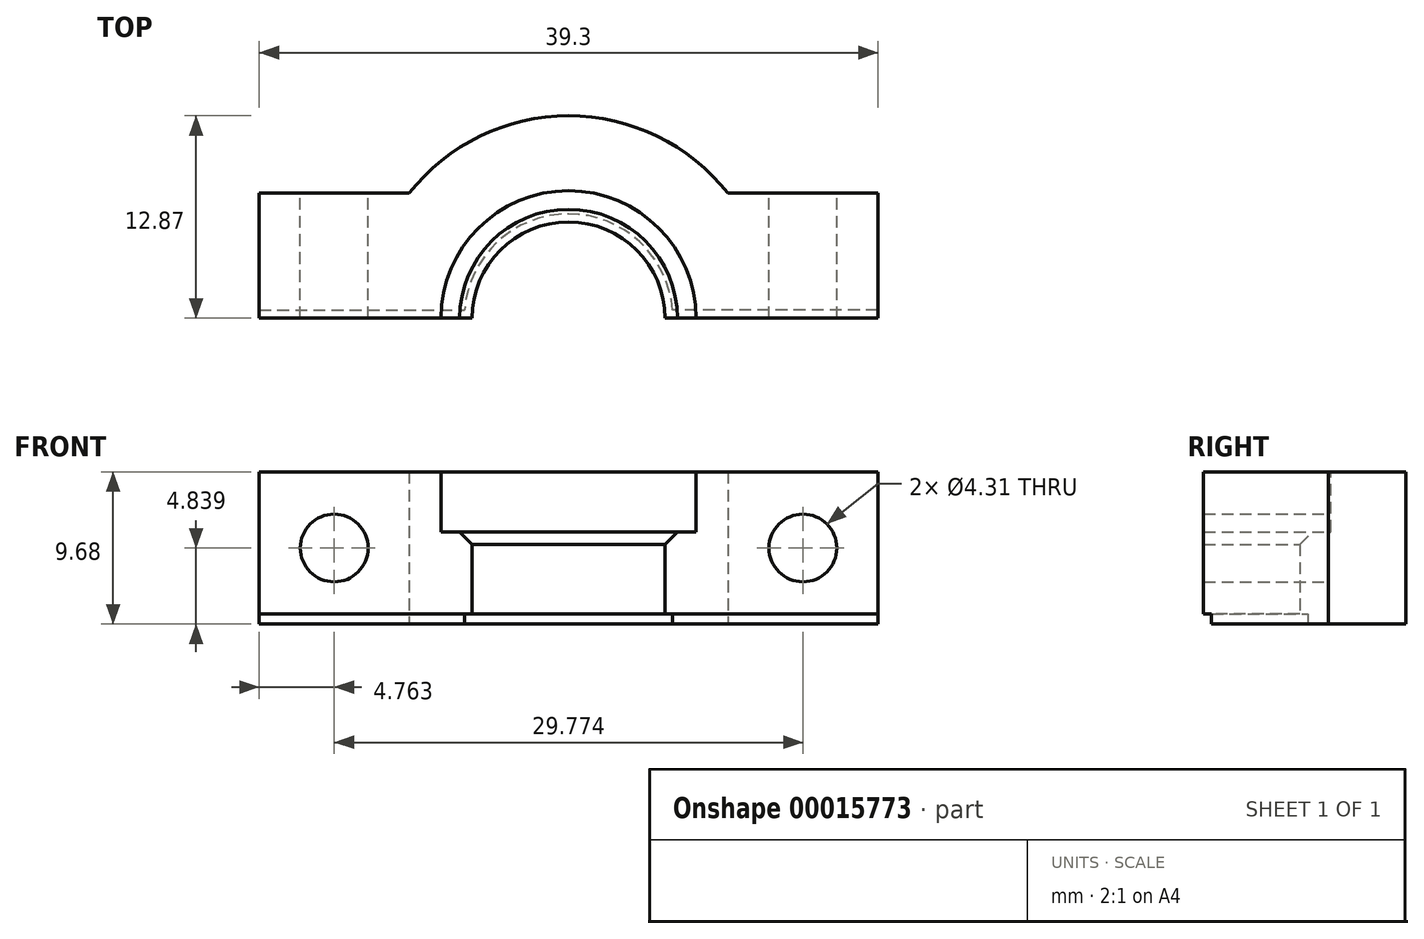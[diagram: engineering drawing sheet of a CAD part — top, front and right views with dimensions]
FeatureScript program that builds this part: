
annotation { "Feature Type Name" : "Feature", "Feature Type Description" : "" }
export const myFeature = defineFeature(function(context is Context, id is Id, definition is map)
    precondition{}
    {
        {
            var Q0;
            Q0=qCreatedBy(makeId("Top.planeOp"),FACE);
            var sketch = newSketch(context, id + "F0", { "sketchPlane" : qUnion([Q0])});
            skArc(sketch, "E0", {"start": v(10.12, 7.94) * mm, "mid": v(0, 12.87) * mm, "end": v(-10.12, 7.94) * mm});
            skLineSegment(sketch, "E1", {"start": v(10.12, 7.94) * mm, "end": v(19.65, 7.94) * mm});
            skLineSegment(sketch, "E2", {"start": v(19.65, 7.94) * mm, "end": v(19.65, 0) * mm});
            skLineSegment(sketch, "E3", {"start": v(19.65, 0) * mm, "end": v(6.12, 0) * mm});
            skLineSegment(sketch, "E4", {"start": v(-10.12, 7.94) * mm, "end": v(-19.65, 7.94) * mm});
            skLineSegment(sketch, "E5", {"start": v(-19.65, 7.94) * mm, "end": v(-19.65, 0) * mm});
            skLineSegment(sketch, "E6", {"start": v(-19.65, 0) * mm, "end": v(-6.12, 0) * mm});
            skArc(sketch, "E7", {"start": v(6.12, 0) * mm, "mid": v(0, 6.12) * mm, "end": v(-6.12, 0) * mm});
            skLineSegment(sketch, "E8", {"start": v(6.12, 0) * mm, "end": v(-6.12, 0) * mm, "construction": true});
            skSolve(sketch);
        }
        {
            var Q0;
            Q0=qSketchRegion(id+"F0",true);
            extrude(context, id + "F1", {"entities" : qUnion([Q0]), "depth" : 9.68 * mm});
        }
        {
            var Q0;
            Q0=makeQuery(id+"F1.opExtrude","CAP_FACE",FACE,{"disambiguationData":[OSD([sQuery(id+"F0.wireOp",EDGE,"E0"),sQuery(id+"F0.wireOp",EDGE,"E1"),sQuery(id+"F0.wireOp",EDGE,"E2"),sQuery(id+"F0.wireOp",EDGE,"E3"),sQuery(id+"F0.wireOp",EDGE,"E4"),sQuery(id+"F0.wireOp",EDGE,"E5"),sQuery(id+"F0.wireOp",EDGE,"E6"),sQuery(id+"F0.wireOp",EDGE,"E7")])],"isStart":false});
            var sketch = newSketch(context, id + "F2", { "sketchPlane" : qUnion([Q0])});
            skArc(sketch, "E9", {"start": v(8.1, 0) * mm, "mid": v(0, 8.1) * mm, "end": v(-8.1, 0) * mm});
            skLineSegment(sketch, "E10", {"start": v(-8.1, 0) * mm, "end": v(8.1, 0) * mm});
            skSolve(sketch);
        }
        {
            var Q0;
            Q0=qSketchRegion(id+"F2",true);
            extrude(context, id + "F3", {"entities" : qUnion([Q0]), "operationType" : NewBodyOperationType.REMOVE, "oppositeDirection" : true, "depth" : 3.8 * mm});
        }
        {
            var Q0;
            Q0=makeQuery(id+"Fcnf6DAoSrvQHXy_1.boolean.opBoolean","MERGE",FACE,{"derivedFrom":[makeQuery(id+"F1.opExtrude","SWEPT_FACE",FACE,{"disambiguationData":[OSD([sQuery(id+"F0.wireOp",EDGE,"E1")])]}),makeQuery(id+"Fcnf6DAoSrvQHXy_1.opExtrude","SWEPT_FACE",FACE,{"disambiguationData":[OSD([sQuery(id+"FU0dKYhuMv5mhTu_1.wireOp",EDGE,"dufKjFn1-3u80-6kKx-2Lr4-ypfS1irZzG7M.bottom")])]})]});
            var sketch = newSketch(context, id + "F4", { "sketchPlane" : qUnion([Q0])});
            skLineSegment(sketch, "E11", {"start": v(-19.65, 4.84) * mm, "end": v(-14.89, 4.84) * mm, "construction": true});
            skLineSegment(sketch, "E12", {"start": v(-14.89, 4.84) * mm, "end": v(14.89, 4.84) * mm, "construction": true});
            skLineSegment(sketch, "E13", {"start": v(14.89, 4.84) * mm, "end": v(19.65, 4.84) * mm, "construction": true});
            skCircle(sketch, "E14", {"center": v(-14.89, 4.84) * mm, "radius": 2.15 * mm});
            skCircle(sketch, "E15", {"center": v(14.89, 4.84) * mm, "radius": 2.15 * mm});
            skSolve(sketch);
        }
        {
            var Q0;
            Q0=qSketchRegion(id+"F4",true);
            var Q1;
            Q1=makeQuery(id+"Fcnf6DAoSrvQHXy_1.boolean.opBoolean","MERGE",FACE,{"derivedFrom":[makeQuery(id+"F1.opExtrude","SWEPT_FACE",FACE,{"disambiguationData":[OSD([sQuery(id+"F0.wireOp",EDGE,"E3")])]}),makeQuery(id+"Fcnf6DAoSrvQHXy_1.opExtrude","SWEPT_FACE",FACE,{"disambiguationData":[OSD([sQuery(id+"FU0dKYhuMv5mhTu_1.wireOp",EDGE,"dufKjFn1-3u80-6kKx-2Lr4-ypfS1irZzG7M.top")])]})]});
            extrude(context, id + "F5", {"entities" : qUnion([Q0]), "operationType" : NewBodyOperationType.REMOVE, "endBound" : BoundingType.UP_TO_SURFACE, "oppositeDirection" : true, "endBoundEntityFace" : qUnion([Q1]), "depth" : 25.4 * mm});
        }
        {
            var Q0;
            Q0=makeQuery(id+"F3.boolean.opBoolean","INTERSECT",EDGE,{"derivedFrom":[makeQuery(id+"Fcnf6DAoSrvQHXy_1.boolean.opBoolean","MERGE",FACE,{"derivedFrom":[makeQuery(id+"F1.opExtrude","SWEPT_FACE",FACE,{"disambiguationData":[OSD([sQuery(id+"F0.wireOp",EDGE,"E7")])]}),makeQuery(id+"Fcnf6DAoSrvQHXy_1.opExtrude","SWEPT_FACE",FACE,{"disambiguationData":[OSD([sQuery(id+"FU0dKYhuMv5mhTu_1.wireOp",EDGE,"G2EkEaK5-VPGA-WDTy-kBex-Va6pReq7cfdc")])]})]}),makeQuery(id+"F3.opExtrude","CAP_FACE",FACE,{"disambiguationData":[OSD([sQuery(id+"F2.wireOp",EDGE,"E9"),sQuery(id+"F2.wireOp",EDGE,"E10")])],"isStart":false})]});
            chamfer(context, id + "F6", {"entities" : qUnion([Q0]), "width" : 0.8 * mm, "tangentPropagation" : true});
        }
        {
            var Q0;
            Q0=makeQuery(id+"F1.opExtrude","CAP_FACE",FACE,{"disambiguationData":[OSD([sQuery(id+"F0.wireOp",EDGE,"CiwzOh9S-gjh2-u7K0-iYqr-4pyKjaaiFy5M"),sQuery(id+"F0.wireOp",EDGE,"mwzENWsw-swMQ-uu2A-3sRn-1XFwxnVmSRLX"),sQuery(id+"F0.wireOp",EDGE,"CWwLYLnV-yV6d-huHf-MTXW-Q0aip5A1B8be.left"),sQuery(id+"F0.wireOp",EDGE,"CWwLYLnV-yV6d-huHf-MTXW-Q0aip5A1B8be.right"),sQuery(id+"F0.wireOp",EDGE,"O6FR0lGG-LKvT-cJZV-t96G-iVc7o2wLJRpf.bottom"),sQuery(id+"F0.wireOp",EDGE,"O6FR0lGG-LKvT-cJZV-t96G-iVc7o2wLJRpf.top"),sQuery(id+"F0.wireOp",EDGE,"j7DDFDeq-ND7J-u6Q6-OJYu-UmNp6OXHeJ2o.bottom"),sQuery(id+"F0.wireOp",EDGE,"j7DDFDeq-ND7J-u6Q6-OJYu-UmNp6OXHeJ2o.top"),sQuery(id+"F0.wireOp",EDGE,"to8QZ3h0-cueq-176H-aO6l-EC2qiW8lXA0D"),sQuery(id+"F0.wireOp",EDGE,"9Ib7JDXT-Hn98-4XN4-feaL-rfxdtM7HG8Y3"),sQuery(id+"F0.wireOp",EDGE,"PW1jYjeF-7eFG-3ugl-4o9v-lLWyo6NCxzAr"),sQuery(id+"F0.wireOp",EDGE,"E0"),sQuery(id+"F0.wireOp",EDGE,"xZv9hLdD-BYe2-NpfH-B7S9-T5A952xZV9do"),sQuery(id+"F0.wireOp",EDGE,"E1"),sQuery(id+"F0.wireOp",EDGE,"E2"),sQuery(id+"F0.wireOp",EDGE,"E3"),sQuery(id+"F0.wireOp",EDGE,"E4"),sQuery(id+"F0.wireOp",EDGE,"E5"),sQuery(id+"F0.wireOp",EDGE,"E6"),sQuery(id+"F0.wireOp",EDGE,"E7")])],"isStart":true});
            var sketch = newSketch(context, id + "F7", { "sketchPlane" : qUnion([Q0])});
            skLineSegment(sketch, "E16.bottom", {"start": v(-19.65, 0) * mm, "end": v(-6.12, 0) * mm});
            skLineSegment(sketch, "E16.top", {"start": v(-19.65, -0.5) * mm, "end": v(-6.6, -0.5) * mm});
            skLineSegment(sketch, "E16.left", {"start": v(-19.65, 0) * mm, "end": v(-19.65, -0.5) * mm});
            skLineSegment(sketch, "E17.bottom", {"start": v(19.65, 0) * mm, "end": v(6.12, 0) * mm});
            skLineSegment(sketch, "E17.top", {"start": v(19.65, -0.5) * mm, "end": v(6.6, -0.5) * mm});
            skLineSegment(sketch, "E17.left", {"start": v(19.65, 0) * mm, "end": v(19.65, -0.5) * mm});
            skArc(sketch, "E18", {"start": v(-6.12, 0) * mm, "mid": v(0, -6.12) * mm, "end": v(6.12, 0) * mm});
            skArc(sketch, "E19", {"start": v(-6.6, -0.5) * mm, "mid": v(0, -6.63) * mm, "end": v(6.6, -0.5) * mm});
            skSolve(sketch);
        }
        {
            var Q0;
            Q0=qSketchRegion(id+"F7",true);
            extrude(context, id + "F8", {"entities" : qUnion([Q0]), "operationType" : NewBodyOperationType.REMOVE, "oppositeDirection" : true, "depth" : 0.64 * mm});
        }
    });
